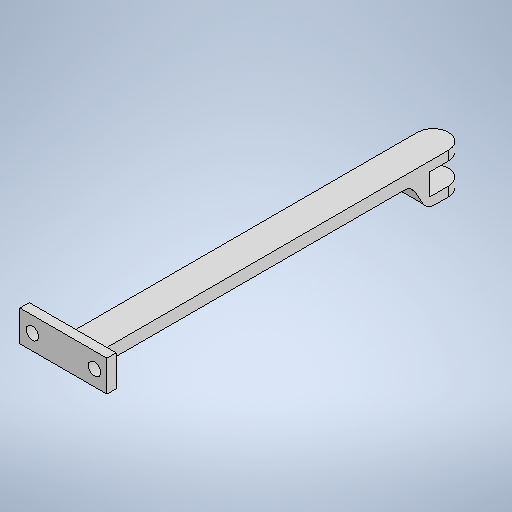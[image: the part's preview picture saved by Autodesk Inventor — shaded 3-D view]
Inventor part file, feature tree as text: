
AUTODESK INVENTOR PART (.ipt)
format: ipt  version: 2025 (Build 290162010, 162A)  size: 302,592 bytes
history: native  units: mm
features: sketch x3, extrude x2, fillet x2, plane x1, hole x1, projected_geometry x1
ambient origin geometry x8: Origin, YZ Plane, XZ Plane, XY Plane, X Axis, Y Axis, Z Axis, Center Point
bodies: Body1 (feature_tree)
feature tree (10):
  sketch  "Sketch5"  dims[d29=3.0mm d30=7.0mm d31=3.0mm d33=11.0mm]
  plane  "Work Plane1"
  extrude  "Extrusion5"  Depth=7.0mm
  fillet  "Fillet1"  Radius=3.0mm
  fillet  "Fillet2"  Radius=11.0mm
  extrude  "Extrusion6"  Depth=5.0mm
  hole  "Hole3"  [1 undecoded]
  sketch  "Sketch7"  dims[d40=4.0mm d41=5.0mm]
  projected_geometry  "Projected Loop1"
  sketch  "Sketch8"  dims[d44=0.0mm d48=12.0mm d53=121.0mm d54=10.0mm d55=0.0mm d56=5.0mm d57=4.0mm d58=28.0mm d59=3.0mm d60=10.0mm d61=0.0mm d62=4.0mm d63=6.0mm d64=4.0mm d65=2.0mm d66=90.0deg d67=8.0mm d68=0.0mm d69=4.0mm d70=4.0mm]
note: 1 required parameter value undecoded (feature->parameter linkage not recoverable at this tier; creation-order binding heuristic only, values carry confidence <= 0.55)
